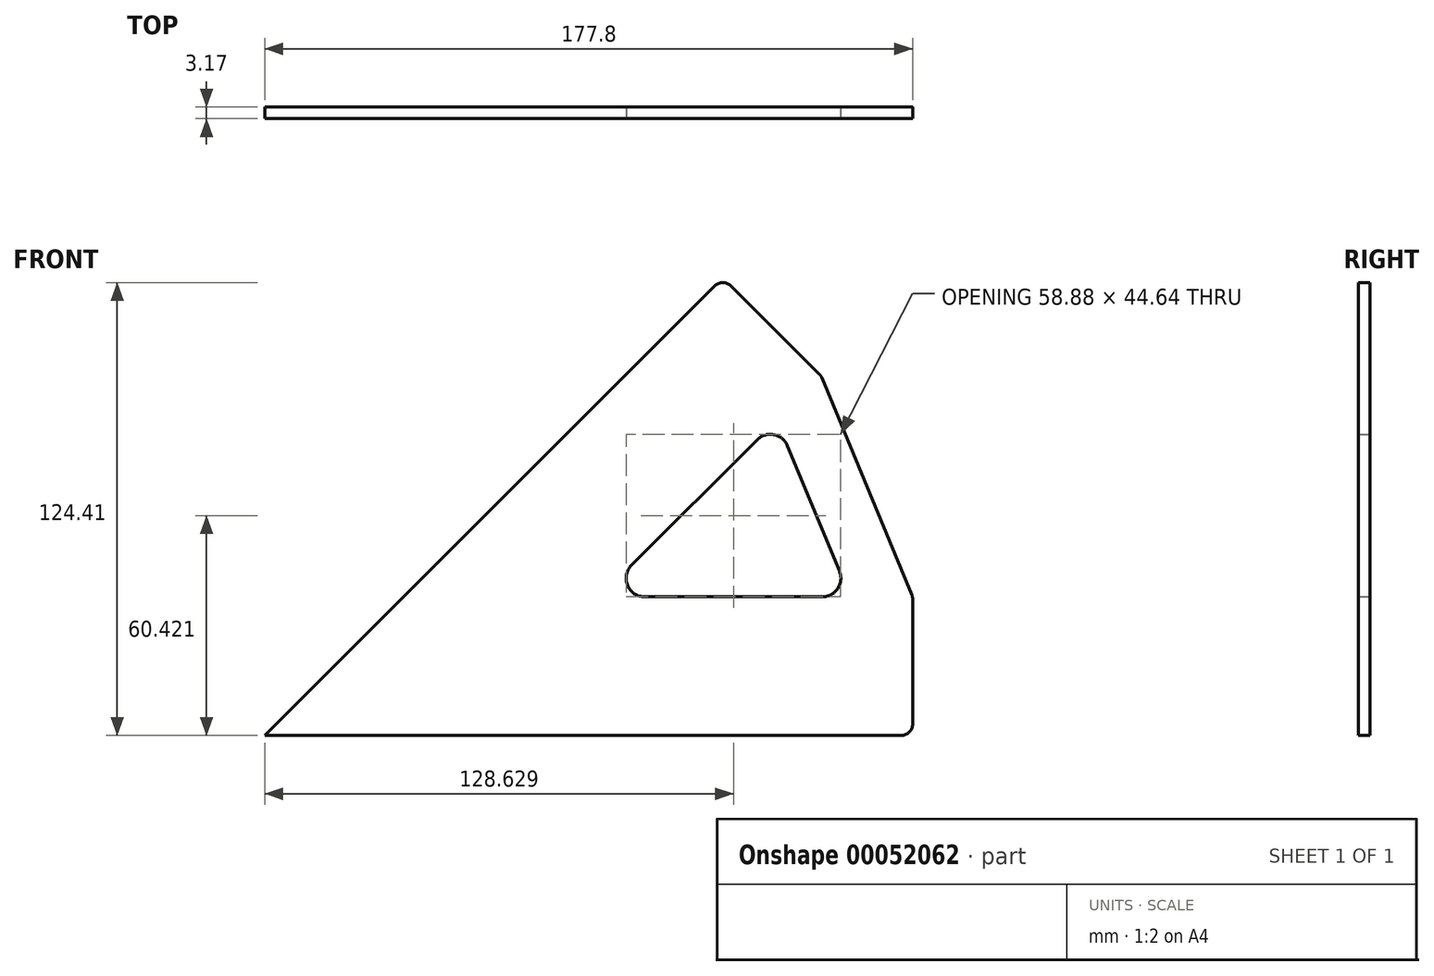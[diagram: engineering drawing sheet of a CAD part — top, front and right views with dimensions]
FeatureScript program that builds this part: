
annotation { "Feature Type Name" : "Feature", "Feature Type Description" : "" }
export const myFeature = defineFeature(function(context is Context, id is Id, definition is map)
    precondition{}
    {
        {
            var Q0;
            Q0=qCreatedBy(makeId("Front.planeOp"),FACE);
            var sketch = newSketch(context, id + "F0", { "sketchPlane" : qUnion([Q0])});
            skLineSegment(sketch, "E0", {"start": v(-84.1, -11.18) * mm, "end": v(93.7, -11.18) * mm});
            skLineSegment(sketch, "E1", {"start": v(93.7, -11.18) * mm, "end": v(93.7, 26.92) * mm});
            skLineSegment(sketch, "E2", {"start": v(-84.1, -11.18) * mm, "end": v(41.63, 114.55) * mm});
            skLineSegment(sketch, "E3", {"start": v(41.63, 114.55) * mm, "end": v(68.57, 87.6) * mm});
            skLineSegment(sketch, "E4", {"start": v(56.42, 75.45) * mm, "end": v(7.9, 26.92) * mm});
            skLineSegment(sketch, "E5", {"start": v(7.9, 26.92) * mm, "end": v(76.53, 26.92) * mm});
            skLineSegment(sketch, "E6", {"start": v(68.57, 87.6) * mm, "end": v(93.7, 26.92) * mm});
            skLineSegment(sketch, "E7", {"start": v(56.42, 75.45) * mm, "end": v(76.53, 26.92) * mm});
            skSolve(sketch);
        }
        {
            var Q0;
            Q0=makeQuery(id+"F0.imprint","IMPRINT",FACE,{"disambiguationData":[TD([[makeQuery(id+"F0.imprint","IMPRINT",EDGE,{"derivedFrom":sQuery(id+"F0.wireOp",EDGE,"E0")}),1.0]])]});
            extrude(context, id + "F1", {"entities" : qUnion([Q0]), "depth" : 3.17 * mm});
        }
        {
            var Q0;
            Q0=makeQuery(id+"F1.opExtrude","SWEPT_EDGE",EDGE,{"disambiguationData":[OSD([sQuery(id+"F0.wireOp",EDGE,"E4"),sQuery(id+"F0.wireOp",EDGE,"E5")])]});
            var Q1;
            Q1=makeQuery(id+"F1.opExtrude","SWEPT_EDGE",EDGE,{"disambiguationData":[OSD([sQuery(id+"F0.wireOp",EDGE,"E5"),sQuery(id+"F0.wireOp",EDGE,"E7")])]});
            var Q2;
            Q2=makeQuery(id+"F1.opExtrude","SWEPT_EDGE",EDGE,{"disambiguationData":[OSD([sQuery(id+"F0.wireOp",EDGE,"E4"),sQuery(id+"F0.wireOp",EDGE,"E7")])]});
            fillet(context, id + "F2", {"entities" : qUnion([Q0, Q1, Q2]), "radius" : 5.08 * mm, "tangentPropagation" : true, "allowEdgeOverflow" : false});
        }
        {
            var Q0;
            Q0=makeQuery(id+"F1.opExtrude","SWEPT_EDGE",EDGE,{"disambiguationData":[OSD([sQuery(id+"F0.wireOp",EDGE,"E2"),sQuery(id+"F0.wireOp",EDGE,"E3")])]});
            var Q1;
            Q1=makeQuery(id+"F1.opExtrude","SWEPT_EDGE",EDGE,{"disambiguationData":[OSD([sQuery(id+"F0.wireOp",EDGE,"E3"),sQuery(id+"F0.wireOp",EDGE,"E6")])]});
            var Q2;
            Q2=makeQuery(id+"F1.opExtrude","SWEPT_EDGE",EDGE,{"disambiguationData":[OSD([sQuery(id+"F0.wireOp",EDGE,"E1"),sQuery(id+"F0.wireOp",EDGE,"E6")])]});
            var Q3;
            Q3=makeQuery(id+"F1.opExtrude","SWEPT_EDGE",EDGE,{"disambiguationData":[OSD([sQuery(id+"F0.wireOp",EDGE,"E0"),sQuery(id+"F0.wireOp",EDGE,"E1")])]});
            fillet(context, id + "F3", {"entities" : qUnion([Q0, Q1, Q2, Q3]), "radius" : 3.17 * mm, "tangentPropagation" : true, "allowEdgeOverflow" : false});
        }
    });
